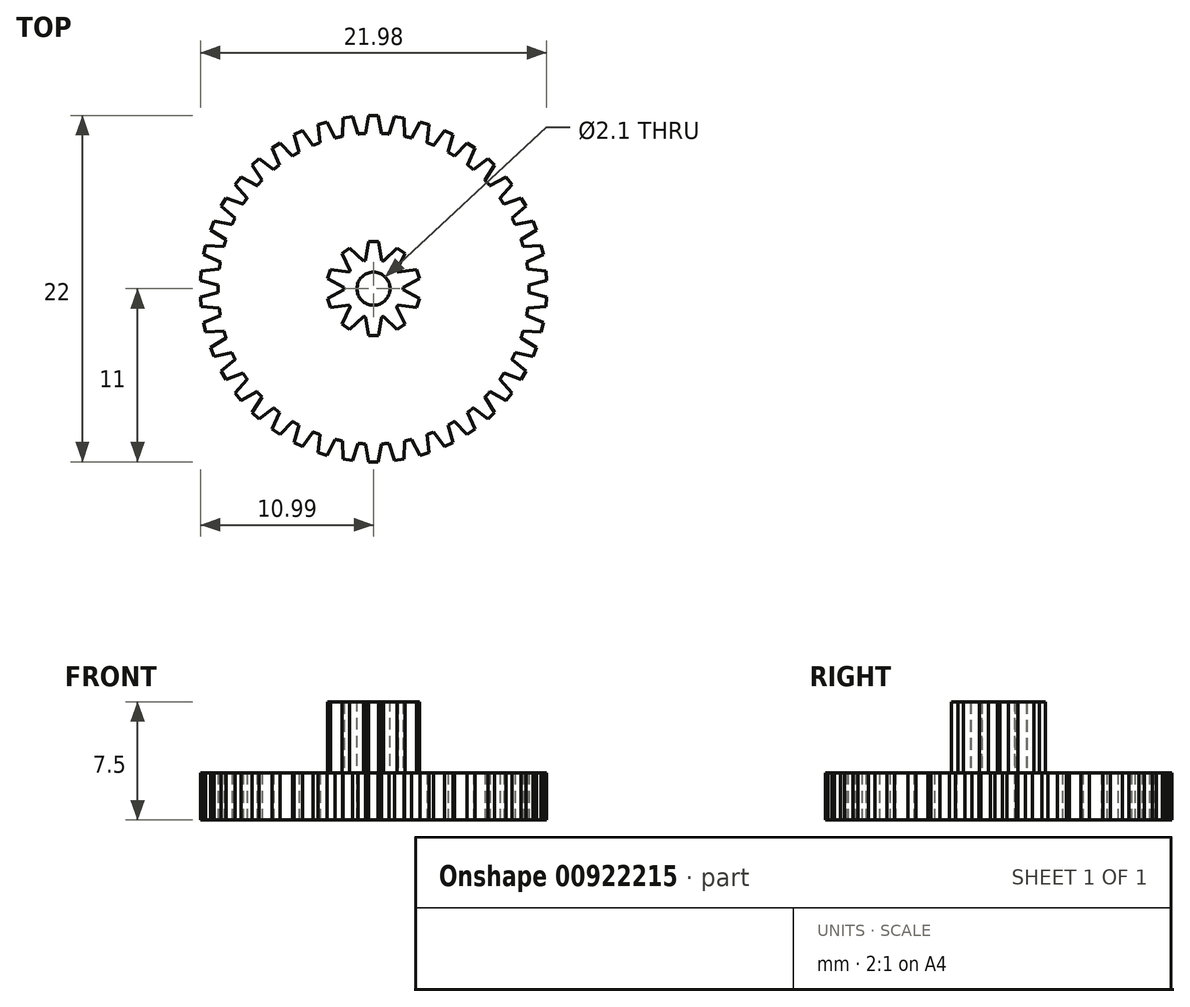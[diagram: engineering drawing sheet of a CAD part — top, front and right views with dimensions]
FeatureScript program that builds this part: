
annotation { "Feature Type Name" : "Feature", "Feature Type Description" : "" }
export const myFeature = defineFeature(function(context is Context, id is Id, definition is map)
    precondition{}
    {
        {
            var Q0;
            Q0=qCreatedBy(makeId("Top.planeOp"),FACE);
            var sketch = newSketch(context, id + "F0", { "sketchPlane" : qUnion([Q0])});
            skCircle(sketch, "E0", {"center": v(0, 0) * mm, "radius": 10.5 * mm, "construction": true});
            skCircle(sketch, "E1", {"center": v(0, 0) * mm, "radius": 11 * mm, "construction": true});
            skCircle(sketch, "E2", {"center": v(0, 0) * mm, "radius": 9.88 * mm});
            skLineSegment(sketch, "E3", {"start": v(0, 9.88) * mm, "end": v(0.5, 9.88) * mm, "construction": true});
            skLineSegment(sketch, "E4", {"start": v(0, 9.88) * mm, "end": v(-0.5, 9.88) * mm, "construction": true});
            skLineSegment(sketch, "E5", {"start": v(-1.02, 6.93) * mm, "end": v(-0.5, 9.86) * mm, "construction": true});
            skLineSegment(sketch, "E6", {"start": v(1.02, 6.94) * mm, "end": v(0.3, 11) * mm, "construction": true});
            skLineSegment(sketch, "E7", {"start": v(-1.02, 6.94) * mm, "end": v(-0.3, 11) * mm});
            skLineSegment(sketch, "E8", {"start": v(0.3, 11) * mm, "end": v(-0.3, 11) * mm});
            skLineSegment(sketch, "E9", {"start": v(0.3, 11) * mm, "end": v(0.5, 9.86) * mm});
            skLineSegment(sketch, "E10.1.0", {"start": v(-2.04, 6.71) * mm, "end": v(-1.94, 10.83) * mm});
            skLineSegment(sketch, "E10.1.1", {"start": v(-1.34, 10.92) * mm, "end": v(-1.94, 10.83) * mm});
            skLineSegment(sketch, "E10.1.2", {"start": v(-1.34, 10.92) * mm, "end": v(-0.97, 9.83) * mm});
            skLineSegment(sketch, "E10.2.0", {"start": v(-3.02, 6.34) * mm, "end": v(-3.53, 10.42) * mm});
            skLineSegment(sketch, "E10.2.1", {"start": v(-2.95, 10.6) * mm, "end": v(-3.53, 10.42) * mm});
            skLineSegment(sketch, "E10.2.2", {"start": v(-2.95, 10.6) * mm, "end": v(-2.43, 9.57) * mm});
            skLineSegment(sketch, "E11.1.3.0", {"start": v(-3.93, 5.81) * mm, "end": v(-5.04, 9.78) * mm});
            skLineSegment(sketch, "E11.3.3.0", {"start": v(-4.5, 10.04) * mm, "end": v(-5.04, 9.78) * mm});
            skLineSegment(sketch, "E11.6.3.0", {"start": v(-4.5, 10.04) * mm, "end": v(-3.83, 9.1) * mm});
            skLineSegment(sketch, "E11.1.4.0", {"start": v(-4.75, 5.16) * mm, "end": v(-6.44, 8.91) * mm});
            skLineSegment(sketch, "E11.3.4.0", {"start": v(-5.94, 9.26) * mm, "end": v(-6.44, 8.91) * mm});
            skLineSegment(sketch, "E11.6.4.0", {"start": v(-5.94, 9.26) * mm, "end": v(-5.14, 8.43) * mm});
            skLineSegment(sketch, "E11.1.5.0", {"start": v(-5.47, 4.4) * mm, "end": v(-7.7, 7.85) * mm});
            skLineSegment(sketch, "E11.3.5.0", {"start": v(-7.26, 8.27) * mm, "end": v(-7.7, 7.85) * mm});
            skLineSegment(sketch, "E11.6.5.0", {"start": v(-7.26, 8.27) * mm, "end": v(-6.34, 7.57) * mm});
            skLineSegment(sketch, "E11.1.6.0", {"start": v(-6.06, 3.53) * mm, "end": v(-8.79, 6.62) * mm});
            skLineSegment(sketch, "E11.3.6.0", {"start": v(-8.4, 7.1) * mm, "end": v(-8.79, 6.62) * mm});
            skLineSegment(sketch, "E11.6.6.0", {"start": v(-8.4, 7.1) * mm, "end": v(-7.4, 6.54) * mm});
            skLineSegment(sketch, "E11.1.7.0", {"start": v(-6.52, 2.6) * mm, "end": v(-9.67, 5.24) * mm});
            skLineSegment(sketch, "E11.3.7.0", {"start": v(-9.37, 5.76) * mm, "end": v(-9.67, 5.24) * mm});
            skLineSegment(sketch, "E11.6.7.0", {"start": v(-9.37, 5.76) * mm, "end": v(-8.29, 5.37) * mm});
            skLineSegment(sketch, "E11.1.8.0", {"start": v(-6.84, 1.6) * mm, "end": v(-10.35, 3.74) * mm});
            skLineSegment(sketch, "E11.3.8.0", {"start": v(-10.13, 4.3) * mm, "end": v(-10.35, 3.74) * mm});
            skLineSegment(sketch, "E11.6.8.0", {"start": v(-10.13, 4.3) * mm, "end": v(-9, 4.07) * mm});
            skLineSegment(sketch, "E11.1.9.0", {"start": v(-7, 0.55) * mm, "end": v(-10.79, 2.15) * mm});
            skLineSegment(sketch, "E11.3.9.0", {"start": v(-10.65, 2.74) * mm, "end": v(-10.79, 2.15) * mm});
            skLineSegment(sketch, "E11.6.9.0", {"start": v(-10.65, 2.74) * mm, "end": v(-9.5, 2.68) * mm});
            skLineSegment(sketch, "E11.1.10.0", {"start": v(-7, -0.5) * mm, "end": v(-10.99, 0.52) * mm});
            skLineSegment(sketch, "E11.3.10.0", {"start": v(-10.94, 1.12) * mm, "end": v(-10.99, 0.52) * mm});
            skLineSegment(sketch, "E11.6.10.0", {"start": v(-10.94, 1.12) * mm, "end": v(-9.8, 1.24) * mm});
            skLineSegment(sketch, "E11.1.11.0", {"start": v(-6.85, -1.53) * mm, "end": v(-10.94, -1.12) * mm});
            skLineSegment(sketch, "E11.3.11.0", {"start": v(-10.99, -0.52) * mm, "end": v(-10.94, -1.12) * mm});
            skLineSegment(sketch, "E11.6.11.0", {"start": v(-10.99, -0.52) * mm, "end": v(-9.87, -0.24) * mm});
            skLineSegment(sketch, "E11.1.12.0", {"start": v(-6.54, -2.54) * mm, "end": v(-10.65, -2.74) * mm});
            skLineSegment(sketch, "E11.3.12.0", {"start": v(-10.79, -2.15) * mm, "end": v(-10.65, -2.74) * mm});
            skLineSegment(sketch, "E11.6.12.0", {"start": v(-10.79, -2.15) * mm, "end": v(-9.73, -1.7) * mm});
            skLineSegment(sketch, "E11.1.13.0", {"start": v(-6.1, -3.48) * mm, "end": v(-10.13, -4.3) * mm});
            skLineSegment(sketch, "E11.3.13.0", {"start": v(-10.35, -3.74) * mm, "end": v(-10.13, -4.3) * mm});
            skLineSegment(sketch, "E11.6.13.0", {"start": v(-10.35, -3.74) * mm, "end": v(-9.36, -3.14) * mm});
            skLineSegment(sketch, "E11.1.14.0", {"start": v(-5.5, -4.35) * mm, "end": v(-9.37, -5.76) * mm});
            skLineSegment(sketch, "E11.3.14.0", {"start": v(-9.67, -5.24) * mm, "end": v(-9.37, -5.76) * mm});
            skLineSegment(sketch, "E11.6.14.0", {"start": v(-9.67, -5.24) * mm, "end": v(-8.8, -4.5) * mm});
            skLineSegment(sketch, "E11.1.15.0", {"start": v(-4.8, -5.12) * mm, "end": v(-8.4, -7.1) * mm});
            skLineSegment(sketch, "E11.3.15.0", {"start": v(-8.79, -6.62) * mm, "end": v(-8.4, -7.1) * mm});
            skLineSegment(sketch, "E11.6.15.0", {"start": v(-8.79, -6.62) * mm, "end": v(-8.02, -5.76) * mm});
            skLineSegment(sketch, "E11.1.16.0", {"start": v(-3.98, -5.78) * mm, "end": v(-7.26, -8.27) * mm});
            skLineSegment(sketch, "E11.3.16.0", {"start": v(-7.7, -7.85) * mm, "end": v(-7.26, -8.27) * mm});
            skLineSegment(sketch, "E11.6.16.0", {"start": v(-7.7, -7.85) * mm, "end": v(-7.08, -6.89) * mm});
            skLineSegment(sketch, "E11.1.17.0", {"start": v(-3.07, -6.3) * mm, "end": v(-5.94, -9.26) * mm});
            skLineSegment(sketch, "E11.3.17.0", {"start": v(-6.44, -8.91) * mm, "end": v(-5.94, -9.26) * mm});
            skLineSegment(sketch, "E11.6.17.0", {"start": v(-6.44, -8.91) * mm, "end": v(-5.97, -7.87) * mm});
            skLineSegment(sketch, "E11.1.18.0", {"start": v(-2.1, -6.7) * mm, "end": v(-4.5, -10.04) * mm});
            skLineSegment(sketch, "E11.3.18.0", {"start": v(-5.04, -9.78) * mm, "end": v(-4.5, -10.04) * mm});
            skLineSegment(sketch, "E11.6.18.0", {"start": v(-5.04, -9.78) * mm, "end": v(-4.73, -8.67) * mm});
            skLineSegment(sketch, "E11.1.19.0", {"start": v(-1.07, -6.93) * mm, "end": v(-2.95, -10.6) * mm});
            skLineSegment(sketch, "E11.3.19.0", {"start": v(-3.53, -10.42) * mm, "end": v(-2.95, -10.6) * mm});
            skLineSegment(sketch, "E11.6.19.0", {"start": v(-3.53, -10.42) * mm, "end": v(-3.39, -9.28) * mm});
            skLineSegment(sketch, "E11.1.20.0", {"start": v(-0.03, -7.02) * mm, "end": v(-1.34, -10.92) * mm});
            skLineSegment(sketch, "E11.3.20.0", {"start": v(-1.94, -10.83) * mm, "end": v(-1.34, -10.92) * mm});
            skLineSegment(sketch, "E11.6.20.0", {"start": v(-1.94, -10.83) * mm, "end": v(-1.97, -9.68) * mm});
            skLineSegment(sketch, "E11.1.21.0", {"start": v(1.02, -6.94) * mm, "end": v(0.3, -11) * mm});
            skLineSegment(sketch, "E11.3.21.0", {"start": v(-0.3, -11) * mm, "end": v(0.3, -11) * mm});
            skLineSegment(sketch, "E11.6.21.0", {"start": v(-0.3, -11) * mm, "end": v(-0.5, -9.86) * mm});
            skLineSegment(sketch, "E11.1.22.0", {"start": v(2.04, -6.71) * mm, "end": v(1.94, -10.83) * mm});
            skLineSegment(sketch, "E11.3.22.0", {"start": v(1.34, -10.92) * mm, "end": v(1.94, -10.83) * mm});
            skLineSegment(sketch, "E11.6.22.0", {"start": v(1.34, -10.92) * mm, "end": v(0.97, -9.83) * mm});
            skLineSegment(sketch, "E11.1.23.0", {"start": v(3.02, -6.34) * mm, "end": v(3.53, -10.42) * mm});
            skLineSegment(sketch, "E11.3.23.0", {"start": v(2.95, -10.6) * mm, "end": v(3.53, -10.42) * mm});
            skLineSegment(sketch, "E11.6.23.0", {"start": v(2.95, -10.6) * mm, "end": v(2.43, -9.57) * mm});
            skLineSegment(sketch, "E11.1.24.0", {"start": v(3.93, -5.81) * mm, "end": v(5.04, -9.78) * mm});
            skLineSegment(sketch, "E11.3.24.0", {"start": v(4.5, -10.04) * mm, "end": v(5.04, -9.78) * mm});
            skLineSegment(sketch, "E11.6.24.0", {"start": v(4.5, -10.04) * mm, "end": v(3.83, -9.1) * mm});
            skLineSegment(sketch, "E11.1.25.0", {"start": v(4.75, -5.16) * mm, "end": v(6.44, -8.91) * mm});
            skLineSegment(sketch, "E11.3.25.0", {"start": v(5.94, -9.26) * mm, "end": v(6.44, -8.91) * mm});
            skLineSegment(sketch, "E11.6.25.0", {"start": v(5.94, -9.26) * mm, "end": v(5.14, -8.43) * mm});
            skLineSegment(sketch, "E11.1.26.0", {"start": v(5.47, -4.4) * mm, "end": v(7.7, -7.85) * mm});
            skLineSegment(sketch, "E11.3.26.0", {"start": v(7.26, -8.27) * mm, "end": v(7.7, -7.85) * mm});
            skLineSegment(sketch, "E11.6.26.0", {"start": v(7.26, -8.27) * mm, "end": v(6.34, -7.57) * mm});
            skLineSegment(sketch, "E11.1.27.0", {"start": v(6.06, -3.53) * mm, "end": v(8.79, -6.62) * mm});
            skLineSegment(sketch, "E11.3.27.0", {"start": v(8.4, -7.1) * mm, "end": v(8.79, -6.62) * mm});
            skLineSegment(sketch, "E11.6.27.0", {"start": v(8.4, -7.1) * mm, "end": v(7.4, -6.54) * mm});
            skLineSegment(sketch, "E11.1.28.0", {"start": v(6.52, -2.6) * mm, "end": v(9.67, -5.24) * mm});
            skLineSegment(sketch, "E11.3.28.0", {"start": v(9.37, -5.76) * mm, "end": v(9.67, -5.24) * mm});
            skLineSegment(sketch, "E11.6.28.0", {"start": v(9.37, -5.76) * mm, "end": v(8.29, -5.37) * mm});
            skLineSegment(sketch, "E11.1.29.0", {"start": v(6.84, -1.6) * mm, "end": v(10.35, -3.74) * mm});
            skLineSegment(sketch, "E11.3.29.0", {"start": v(10.13, -4.3) * mm, "end": v(10.35, -3.74) * mm});
            skLineSegment(sketch, "E11.6.29.0", {"start": v(10.13, -4.3) * mm, "end": v(9, -4.07) * mm});
            skLineSegment(sketch, "E12.1.30.0", {"start": v(7, -0.55) * mm, "end": v(10.79, -2.15) * mm});
            skLineSegment(sketch, "E12.3.30.0", {"start": v(10.65, -2.74) * mm, "end": v(10.79, -2.15) * mm});
            skLineSegment(sketch, "E12.6.30.0", {"start": v(10.65, -2.74) * mm, "end": v(9.5, -2.68) * mm});
            skLineSegment(sketch, "E12.1.31.0", {"start": v(7, 0.5) * mm, "end": v(10.99, -0.52) * mm});
            skLineSegment(sketch, "E12.3.31.0", {"start": v(10.94, -1.12) * mm, "end": v(10.99, -0.52) * mm});
            skLineSegment(sketch, "E12.6.31.0", {"start": v(10.94, -1.12) * mm, "end": v(9.8, -1.24) * mm});
            skLineSegment(sketch, "E12.1.32.0", {"start": v(6.85, 1.53) * mm, "end": v(10.94, 1.12) * mm});
            skLineSegment(sketch, "E12.3.32.0", {"start": v(10.99, 0.52) * mm, "end": v(10.94, 1.12) * mm});
            skLineSegment(sketch, "E12.6.32.0", {"start": v(10.99, 0.52) * mm, "end": v(9.87, 0.24) * mm});
            skLineSegment(sketch, "E12.1.33.0", {"start": v(6.54, 2.54) * mm, "end": v(10.65, 2.74) * mm});
            skLineSegment(sketch, "E12.3.33.0", {"start": v(10.79, 2.15) * mm, "end": v(10.65, 2.74) * mm});
            skLineSegment(sketch, "E12.6.33.0", {"start": v(10.79, 2.15) * mm, "end": v(9.73, 1.7) * mm});
            skLineSegment(sketch, "E12.1.34.0", {"start": v(6.1, 3.48) * mm, "end": v(10.13, 4.3) * mm});
            skLineSegment(sketch, "E12.3.34.0", {"start": v(10.35, 3.74) * mm, "end": v(10.13, 4.3) * mm});
            skLineSegment(sketch, "E12.6.34.0", {"start": v(10.35, 3.74) * mm, "end": v(9.36, 3.14) * mm});
            skLineSegment(sketch, "E12.1.35.0", {"start": v(5.5, 4.35) * mm, "end": v(9.37, 5.76) * mm});
            skLineSegment(sketch, "E12.3.35.0", {"start": v(9.67, 5.24) * mm, "end": v(9.37, 5.76) * mm});
            skLineSegment(sketch, "E12.6.35.0", {"start": v(9.67, 5.24) * mm, "end": v(8.8, 4.5) * mm});
            skLineSegment(sketch, "E12.1.36.0", {"start": v(4.8, 5.12) * mm, "end": v(8.4, 7.1) * mm});
            skLineSegment(sketch, "E12.3.36.0", {"start": v(8.79, 6.62) * mm, "end": v(8.4, 7.1) * mm});
            skLineSegment(sketch, "E12.6.36.0", {"start": v(8.79, 6.62) * mm, "end": v(8.02, 5.76) * mm});
            skLineSegment(sketch, "E12.1.37.0", {"start": v(3.98, 5.78) * mm, "end": v(7.26, 8.27) * mm});
            skLineSegment(sketch, "E12.3.37.0", {"start": v(7.7, 7.85) * mm, "end": v(7.26, 8.27) * mm});
            skLineSegment(sketch, "E12.6.37.0", {"start": v(7.7, 7.85) * mm, "end": v(7.08, 6.89) * mm});
            skLineSegment(sketch, "E12.1.38.0", {"start": v(3.07, 6.3) * mm, "end": v(5.94, 9.26) * mm});
            skLineSegment(sketch, "E12.3.38.0", {"start": v(6.44, 8.91) * mm, "end": v(5.94, 9.26) * mm});
            skLineSegment(sketch, "E12.6.38.0", {"start": v(6.44, 8.91) * mm, "end": v(5.97, 7.87) * mm});
            skLineSegment(sketch, "E12.1.39.0", {"start": v(2.1, 6.7) * mm, "end": v(4.5, 10.04) * mm});
            skLineSegment(sketch, "E12.3.39.0", {"start": v(5.04, 9.78) * mm, "end": v(4.5, 10.04) * mm});
            skLineSegment(sketch, "E12.6.39.0", {"start": v(5.04, 9.78) * mm, "end": v(4.73, 8.67) * mm});
            skLineSegment(sketch, "E12.1.40.0", {"start": v(1.07, 6.93) * mm, "end": v(2.95, 10.6) * mm});
            skLineSegment(sketch, "E12.3.40.0", {"start": v(3.53, 10.42) * mm, "end": v(2.95, 10.6) * mm});
            skLineSegment(sketch, "E12.6.40.0", {"start": v(3.53, 10.42) * mm, "end": v(3.39, 9.28) * mm});
            skLineSegment(sketch, "E12.1.41.0", {"start": v(0.03, 7.02) * mm, "end": v(1.34, 10.92) * mm});
            skLineSegment(sketch, "E12.3.41.0", {"start": v(1.94, 10.83) * mm, "end": v(1.34, 10.92) * mm});
            skLineSegment(sketch, "E12.6.41.0", {"start": v(1.94, 10.83) * mm, "end": v(1.97, 9.68) * mm});
            skSolve(sketch);
        }
        {
            var Q0;
            Q0=qSketchRegion(id+"F0",true);
            extrude(context, id + "F1", {"entities" : qUnion([Q0]), "depth" : 3 * mm, "offsetDistance" : 25 * mm});
        }
        {
            var Q0;
            Q0=makeQuery(id+"F1.opExtrude","CAP_FACE",FACE,{"disambiguationData":[OSD([sQuery(id+"F0.wireOp",EDGE,"E2"),sQuery(id+"F0.wireOp",EDGE,"E7"),sQuery(id+"F0.wireOp",EDGE,"E8"),sQuery(id+"F0.wireOp",EDGE,"E9"),sQuery(id+"F0.wireOp",EDGE,"E10.1.0"),sQuery(id+"F0.wireOp",EDGE,"E10.1.1"),sQuery(id+"F0.wireOp",EDGE,"E10.1.2"),sQuery(id+"F0.wireOp",EDGE,"E10.2.0"),sQuery(id+"F0.wireOp",EDGE,"E10.2.1"),sQuery(id+"F0.wireOp",EDGE,"E10.2.2"),sQuery(id+"F0.wireOp",EDGE,"E11.1.3.0"),sQuery(id+"F0.wireOp",EDGE,"E11.3.3.0"),sQuery(id+"F0.wireOp",EDGE,"E11.6.3.0"),sQuery(id+"F0.wireOp",EDGE,"E11.1.4.0"),sQuery(id+"F0.wireOp",EDGE,"E11.3.4.0"),sQuery(id+"F0.wireOp",EDGE,"E11.6.4.0"),sQuery(id+"F0.wireOp",EDGE,"E11.1.5.0"),sQuery(id+"F0.wireOp",EDGE,"E11.3.5.0"),sQuery(id+"F0.wireOp",EDGE,"E11.6.5.0"),sQuery(id+"F0.wireOp",EDGE,"E11.1.6.0"),sQuery(id+"F0.wireOp",EDGE,"E11.3.6.0"),sQuery(id+"F0.wireOp",EDGE,"E11.6.6.0"),sQuery(id+"F0.wireOp",EDGE,"E11.1.7.0"),sQuery(id+"F0.wireOp",EDGE,"E11.3.7.0"),sQuery(id+"F0.wireOp",EDGE,"E11.6.7.0"),sQuery(id+"F0.wireOp",EDGE,"E11.1.8.0"),sQuery(id+"F0.wireOp",EDGE,"E11.3.8.0"),sQuery(id+"F0.wireOp",EDGE,"E11.6.8.0"),sQuery(id+"F0.wireOp",EDGE,"E11.1.9.0"),sQuery(id+"F0.wireOp",EDGE,"E11.3.9.0"),sQuery(id+"F0.wireOp",EDGE,"E11.6.9.0"),sQuery(id+"F0.wireOp",EDGE,"E11.1.10.0"),sQuery(id+"F0.wireOp",EDGE,"E11.3.10.0"),sQuery(id+"F0.wireOp",EDGE,"E11.6.10.0"),sQuery(id+"F0.wireOp",EDGE,"E11.1.11.0"),sQuery(id+"F0.wireOp",EDGE,"E11.3.11.0"),sQuery(id+"F0.wireOp",EDGE,"E11.6.11.0"),sQuery(id+"F0.wireOp",EDGE,"E11.1.12.0"),sQuery(id+"F0.wireOp",EDGE,"E11.3.12.0"),sQuery(id+"F0.wireOp",EDGE,"E11.6.12.0"),sQuery(id+"F0.wireOp",EDGE,"E11.1.13.0"),sQuery(id+"F0.wireOp",EDGE,"E11.3.13.0"),sQuery(id+"F0.wireOp",EDGE,"E11.6.13.0"),sQuery(id+"F0.wireOp",EDGE,"E11.1.14.0"),sQuery(id+"F0.wireOp",EDGE,"E11.3.14.0"),sQuery(id+"F0.wireOp",EDGE,"E11.6.14.0"),sQuery(id+"F0.wireOp",EDGE,"E11.1.15.0"),sQuery(id+"F0.wireOp",EDGE,"E11.3.15.0"),sQuery(id+"F0.wireOp",EDGE,"E11.6.15.0"),sQuery(id+"F0.wireOp",EDGE,"E11.1.16.0"),sQuery(id+"F0.wireOp",EDGE,"E11.3.16.0"),sQuery(id+"F0.wireOp",EDGE,"E11.6.16.0"),sQuery(id+"F0.wireOp",EDGE,"E11.1.17.0"),sQuery(id+"F0.wireOp",EDGE,"E11.3.17.0"),sQuery(id+"F0.wireOp",EDGE,"E11.6.17.0"),sQuery(id+"F0.wireOp",EDGE,"E11.1.18.0"),sQuery(id+"F0.wireOp",EDGE,"E11.3.18.0"),sQuery(id+"F0.wireOp",EDGE,"E11.6.18.0"),sQuery(id+"F0.wireOp",EDGE,"E11.1.19.0"),sQuery(id+"F0.wireOp",EDGE,"E11.3.19.0"),sQuery(id+"F0.wireOp",EDGE,"E11.6.19.0"),sQuery(id+"F0.wireOp",EDGE,"E11.1.20.0"),sQuery(id+"F0.wireOp",EDGE,"E11.3.20.0"),sQuery(id+"F0.wireOp",EDGE,"E11.6.20.0"),sQuery(id+"F0.wireOp",EDGE,"E11.1.21.0"),sQuery(id+"F0.wireOp",EDGE,"E11.3.21.0"),sQuery(id+"F0.wireOp",EDGE,"E11.6.21.0"),sQuery(id+"F0.wireOp",EDGE,"E11.1.22.0"),sQuery(id+"F0.wireOp",EDGE,"E11.3.22.0"),sQuery(id+"F0.wireOp",EDGE,"E11.6.22.0"),sQuery(id+"F0.wireOp",EDGE,"E11.1.23.0"),sQuery(id+"F0.wireOp",EDGE,"E11.3.23.0"),sQuery(id+"F0.wireOp",EDGE,"E11.6.23.0"),sQuery(id+"F0.wireOp",EDGE,"E11.1.24.0"),sQuery(id+"F0.wireOp",EDGE,"E11.3.24.0"),sQuery(id+"F0.wireOp",EDGE,"E11.6.24.0"),sQuery(id+"F0.wireOp",EDGE,"E11.1.25.0"),sQuery(id+"F0.wireOp",EDGE,"E11.3.25.0"),sQuery(id+"F0.wireOp",EDGE,"E11.6.25.0"),sQuery(id+"F0.wireOp",EDGE,"E11.1.26.0"),sQuery(id+"F0.wireOp",EDGE,"E11.3.26.0"),sQuery(id+"F0.wireOp",EDGE,"E11.6.26.0"),sQuery(id+"F0.wireOp",EDGE,"E11.1.27.0"),sQuery(id+"F0.wireOp",EDGE,"E11.3.27.0"),sQuery(id+"F0.wireOp",EDGE,"E11.6.27.0"),sQuery(id+"F0.wireOp",EDGE,"E11.1.28.0"),sQuery(id+"F0.wireOp",EDGE,"E11.3.28.0"),sQuery(id+"F0.wireOp",EDGE,"E11.6.28.0"),sQuery(id+"F0.wireOp",EDGE,"E11.1.29.0"),sQuery(id+"F0.wireOp",EDGE,"E11.3.29.0"),sQuery(id+"F0.wireOp",EDGE,"E11.6.29.0")])],"isStart":false});
            var sketch = newSketch(context, id + "F2", { "sketchPlane" : qUnion([Q0])});
            skCircle(sketch, "E13", {"center": v(0, 0) * mm, "radius": 2.5 * mm, "construction": true});
            skCircle(sketch, "E14", {"center": v(0, 0) * mm, "radius": 3 * mm, "construction": true});
            skCircle(sketch, "E15", {"center": v(0, 0) * mm, "radius": 1.88 * mm});
            skLineSegment(sketch, "E16", {"start": v(0, 1.88) * mm, "end": v(0.5, 1.88) * mm, "construction": true});
            skLineSegment(sketch, "E17", {"start": v(0, 1.88) * mm, "end": v(-0.5, 1.88) * mm, "construction": true});
            skLineSegment(sketch, "E18", {"start": v(-0.51, 1.8) * mm, "end": v(-0.3, 2.98) * mm, "construction": true});
            skLineSegment(sketch, "E19", {"start": v(0.51, 1.8) * mm, "end": v(0.3, 2.98) * mm, "construction": true});
            skLineSegment(sketch, "E20", {"start": v(-0.51, 1.8) * mm, "end": v(-0.3, 2.98) * mm});
            skLineSegment(sketch, "E21", {"start": v(0.3, 2.98) * mm, "end": v(-0.3, 2.98) * mm});
            skLineSegment(sketch, "E22", {"start": v(0.3, 2.98) * mm, "end": v(0.51, 1.8) * mm});
            skLineSegment(sketch, "E23.1.0", {"start": v(-1.47, 1.16) * mm, "end": v(-2, 2.24) * mm});
            skLineSegment(sketch, "E23.1.1", {"start": v(-1.5, 2.6) * mm, "end": v(-2, 2.24) * mm});
            skLineSegment(sketch, "E23.1.2", {"start": v(-1.5, 2.6) * mm, "end": v(-0.65, 1.76) * mm});
            skLineSegment(sketch, "E23.2.0", {"start": v(-1.87, 0.07) * mm, "end": v(-2.93, 0.63) * mm});
            skLineSegment(sketch, "E23.2.1", {"start": v(-2.74, 1.21) * mm, "end": v(-2.93, 0.63) * mm});
            skLineSegment(sketch, "E23.2.2", {"start": v(-2.74, 1.21) * mm, "end": v(-1.56, 1.04) * mm});
            skLineSegment(sketch, "E24.1.3.0", {"start": v(-1.56, -1.04) * mm, "end": v(-2.74, -1.21) * mm});
            skLineSegment(sketch, "E24.3.3.0", {"start": v(-2.93, -0.63) * mm, "end": v(-2.74, -1.21) * mm});
            skLineSegment(sketch, "E24.6.3.0", {"start": v(-2.93, -0.63) * mm, "end": v(-1.87, -0.07) * mm});
            skLineSegment(sketch, "E24.1.4.0", {"start": v(-0.65, -1.76) * mm, "end": v(-1.5, -2.6) * mm});
            skLineSegment(sketch, "E24.3.4.0", {"start": v(-2, -2.24) * mm, "end": v(-1.5, -2.6) * mm});
            skLineSegment(sketch, "E24.6.4.0", {"start": v(-2, -2.24) * mm, "end": v(-1.47, -1.16) * mm});
            skLineSegment(sketch, "E24.1.5.0", {"start": v(0.51, -1.8) * mm, "end": v(0.3, -2.98) * mm});
            skLineSegment(sketch, "E24.3.5.0", {"start": v(-0.3, -2.98) * mm, "end": v(0.3, -2.98) * mm});
            skLineSegment(sketch, "E24.6.5.0", {"start": v(-0.3, -2.98) * mm, "end": v(-0.51, -1.8) * mm});
            skLineSegment(sketch, "E24.1.6.0", {"start": v(1.47, -1.16) * mm, "end": v(2, -2.24) * mm});
            skLineSegment(sketch, "E24.3.6.0", {"start": v(1.5, -2.6) * mm, "end": v(2, -2.24) * mm});
            skLineSegment(sketch, "E24.6.6.0", {"start": v(1.5, -2.6) * mm, "end": v(0.65, -1.76) * mm});
            skLineSegment(sketch, "E24.1.7.0", {"start": v(1.87, -0.07) * mm, "end": v(2.93, -0.63) * mm});
            skLineSegment(sketch, "E24.3.7.0", {"start": v(2.74, -1.21) * mm, "end": v(2.93, -0.63) * mm});
            skLineSegment(sketch, "E24.6.7.0", {"start": v(2.74, -1.21) * mm, "end": v(1.56, -1.04) * mm});
            skLineSegment(sketch, "E24.1.8.0", {"start": v(1.56, 1.04) * mm, "end": v(2.74, 1.21) * mm});
            skLineSegment(sketch, "E24.3.8.0", {"start": v(2.93, 0.63) * mm, "end": v(2.74, 1.21) * mm});
            skLineSegment(sketch, "E24.6.8.0", {"start": v(2.93, 0.63) * mm, "end": v(1.87, 0.07) * mm});
            skLineSegment(sketch, "E24.1.9.0", {"start": v(0.65, 1.76) * mm, "end": v(1.5, 2.6) * mm});
            skLineSegment(sketch, "E24.3.9.0", {"start": v(2, 2.24) * mm, "end": v(1.5, 2.6) * mm});
            skLineSegment(sketch, "E24.6.9.0", {"start": v(2, 2.24) * mm, "end": v(1.47, 1.16) * mm});
            skSolve(sketch);
        }
        {
            var Q0;
            Q0=qSketchRegion(id+"F2",true);
            extrude(context, id + "F3", {"entities" : qUnion([Q0]), "operationType" : NewBodyOperationType.ADD, "depth" : 4.5 * mm, "offsetDistance" : 25 * mm});
        }
        {
            var Q0;
            Q0=makeQuery(id+"F3.opExtrude","CAP_FACE",FACE,{"disambiguationData":[OSD([sQuery(id+"F2.wireOp",EDGE,"E15"),sQuery(id+"F2.wireOp",EDGE,"E20"),sQuery(id+"F2.wireOp",EDGE,"E21"),sQuery(id+"F2.wireOp",EDGE,"E22"),sQuery(id+"F2.wireOp",EDGE,"E23.1.0"),sQuery(id+"F2.wireOp",EDGE,"E23.1.1"),sQuery(id+"F2.wireOp",EDGE,"E23.1.2"),sQuery(id+"F2.wireOp",EDGE,"E23.2.0"),sQuery(id+"F2.wireOp",EDGE,"E23.2.1"),sQuery(id+"F2.wireOp",EDGE,"E23.2.2"),sQuery(id+"F2.wireOp",EDGE,"E24.1.3.0"),sQuery(id+"F2.wireOp",EDGE,"E24.3.3.0"),sQuery(id+"F2.wireOp",EDGE,"E24.6.3.0"),sQuery(id+"F2.wireOp",EDGE,"E24.1.4.0"),sQuery(id+"F2.wireOp",EDGE,"E24.3.4.0"),sQuery(id+"F2.wireOp",EDGE,"E24.6.4.0"),sQuery(id+"F2.wireOp",EDGE,"E24.1.5.0"),sQuery(id+"F2.wireOp",EDGE,"E24.3.5.0"),sQuery(id+"F2.wireOp",EDGE,"E24.6.5.0"),sQuery(id+"F2.wireOp",EDGE,"E24.1.6.0"),sQuery(id+"F2.wireOp",EDGE,"E24.3.6.0"),sQuery(id+"F2.wireOp",EDGE,"E24.6.6.0"),sQuery(id+"F2.wireOp",EDGE,"E24.1.7.0"),sQuery(id+"F2.wireOp",EDGE,"E24.3.7.0"),sQuery(id+"F2.wireOp",EDGE,"E24.6.7.0"),sQuery(id+"F2.wireOp",EDGE,"E24.1.8.0"),sQuery(id+"F2.wireOp",EDGE,"E24.3.8.0"),sQuery(id+"F2.wireOp",EDGE,"E24.6.8.0"),sQuery(id+"F2.wireOp",EDGE,"E24.1.9.0"),sQuery(id+"F2.wireOp",EDGE,"E24.3.9.0"),sQuery(id+"F2.wireOp",EDGE,"E24.6.9.0")])],"isStart":false});
            var sketch = newSketch(context, id + "F4", { "sketchPlane" : qUnion([Q0])});
            skCircle(sketch, "E25", {"center": v(0, 0) * mm, "radius": 1.05 * mm});
            skSolve(sketch);
        }
        {
            var Q0;
            Q0=qSketchRegion(id+"F4",true);
            extrude(context, id + "F5", {"entities" : qUnion([Q0]), "operationType" : NewBodyOperationType.REMOVE, "endBound" : BoundingType.THROUGH_ALL, "oppositeDirection" : true, "depth" : 25 * mm, "offsetDistance" : 25 * mm});
        }
    });
